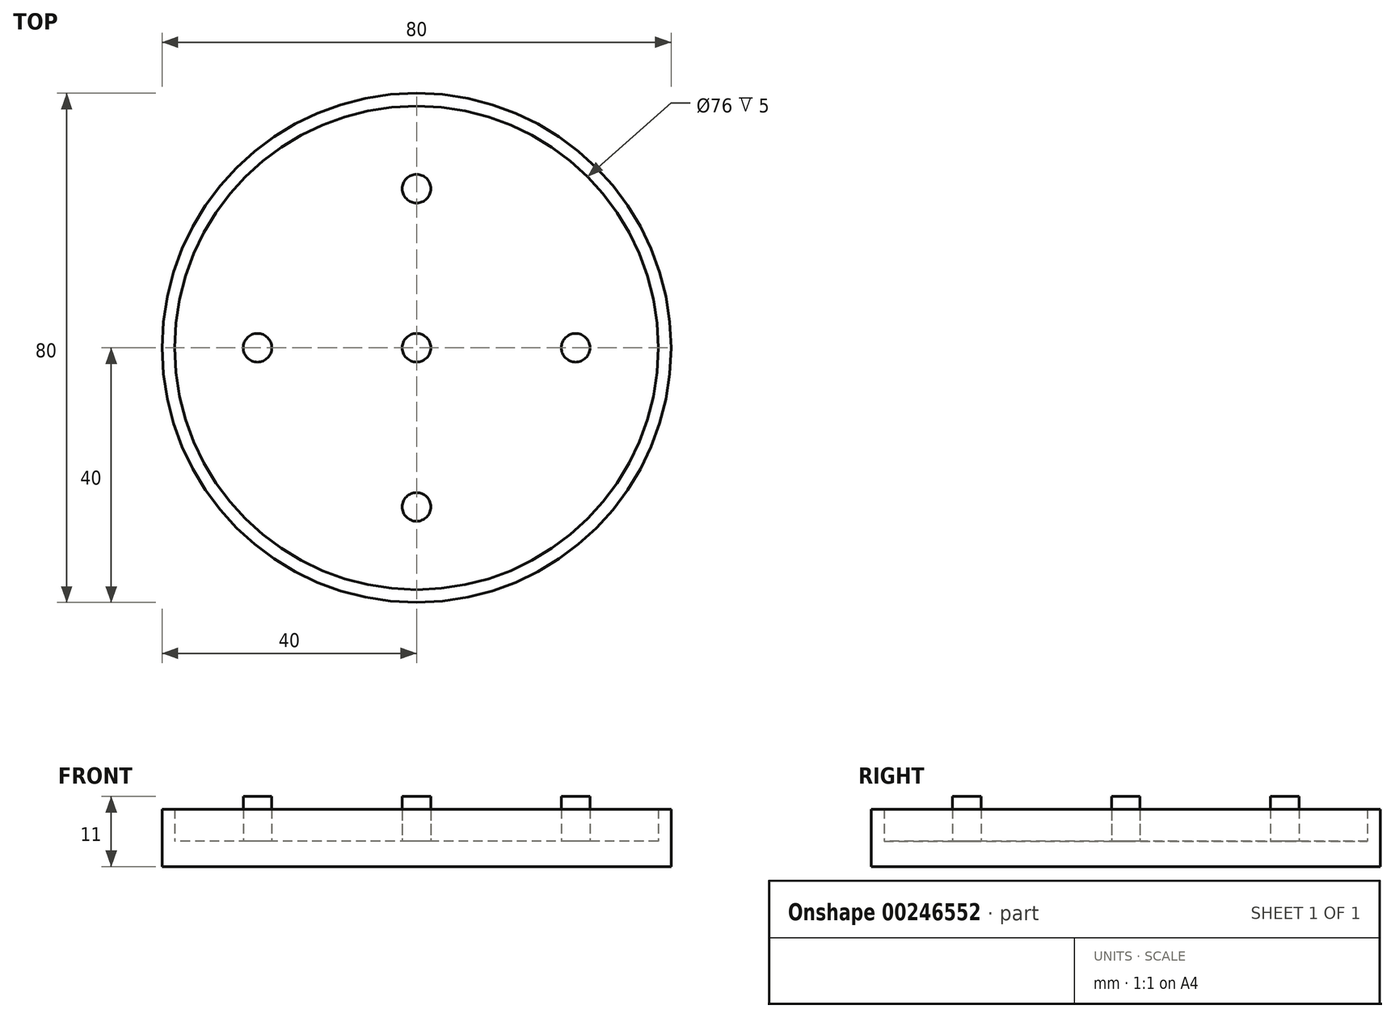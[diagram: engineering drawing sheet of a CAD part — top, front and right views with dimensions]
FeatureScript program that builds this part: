
annotation { "Feature Type Name" : "Feature", "Feature Type Description" : "" }
export const myFeature = defineFeature(function(context is Context, id is Id, definition is map)
    precondition{}
    {
        {
            var Q0;
            Q0=qCreatedBy(makeId("Top.planeOp"),FACE);
            var sketch = newSketch(context, id + "F0", { "sketchPlane" : qUnion([Q0])});
            skCircle(sketch, "E0", {"center": v(0, 0) * mm, "radius": 40 * mm});
            skCircle(sketch, "E1", {"center": v(0, 0) * mm, "radius": 38 * mm});
            skSolve(sketch);
        }
        {
            var Q0;
            Q0=makeQuery(id+"F0.imprint","IMPRINT",FACE,{"disambiguationData":[TD([[makeQuery(id+"F0.imprint","IMPRINT",EDGE,{"derivedFrom":sQuery(id+"F0.wireOp",EDGE,"E0")}),1.0]])]});
            extrude(context, id + "F1", {"entities" : qUnion([Q0]), "depth" : 9 * mm});
        }
        {
            var Q0;
            Q0=makeQuery(id+"F0.imprint","IMPRINT",FACE,{"disambiguationData":[TD([[makeQuery(id+"F0.imprint","IMPRINT",EDGE,{"derivedFrom":sQuery(id+"F0.wireOp",EDGE,"E1")}),1.0]])]});
            extrude(context, id + "F2", {"entities" : qUnion([Q0]), "operationType" : NewBodyOperationType.ADD, "depth" : 4 * mm});
        }
        {
            var Q0;
            Q0=makeQuery(id+"F2.opExtrude","CAP_FACE",FACE,{"disambiguationData":[OSD([sQuery(id+"F0.wireOp",EDGE,"E1")])],"isStart":false});
            var sketch = newSketch(context, id + "F3", { "sketchPlane" : qUnion([Q0])});
            skCircle(sketch, "E2", {"center": v(0, 0) * mm, "radius": 2.25 * mm});
            skCircle(sketch, "E3", {"center": v(-25, 0) * mm, "radius": 2.25 * mm});
            skCircle(sketch, "E4", {"center": v(25, 0) * mm, "radius": 2.25 * mm});
            skCircle(sketch, "E5", {"center": v(0, 25) * mm, "radius": 2.25 * mm});
            skCircle(sketch, "E6", {"center": v(0, -25) * mm, "radius": 2.25 * mm});
            skSolve(sketch);
        }
        {
            var Q0;
            Q0 = qSketchRegion(id + "F3", true);
            extrude(context, id + "F4", {"entities" : qUnion([Q0]), "operationType" : NewBodyOperationType.ADD, "depth" : 7 * mm});
        }
    });
